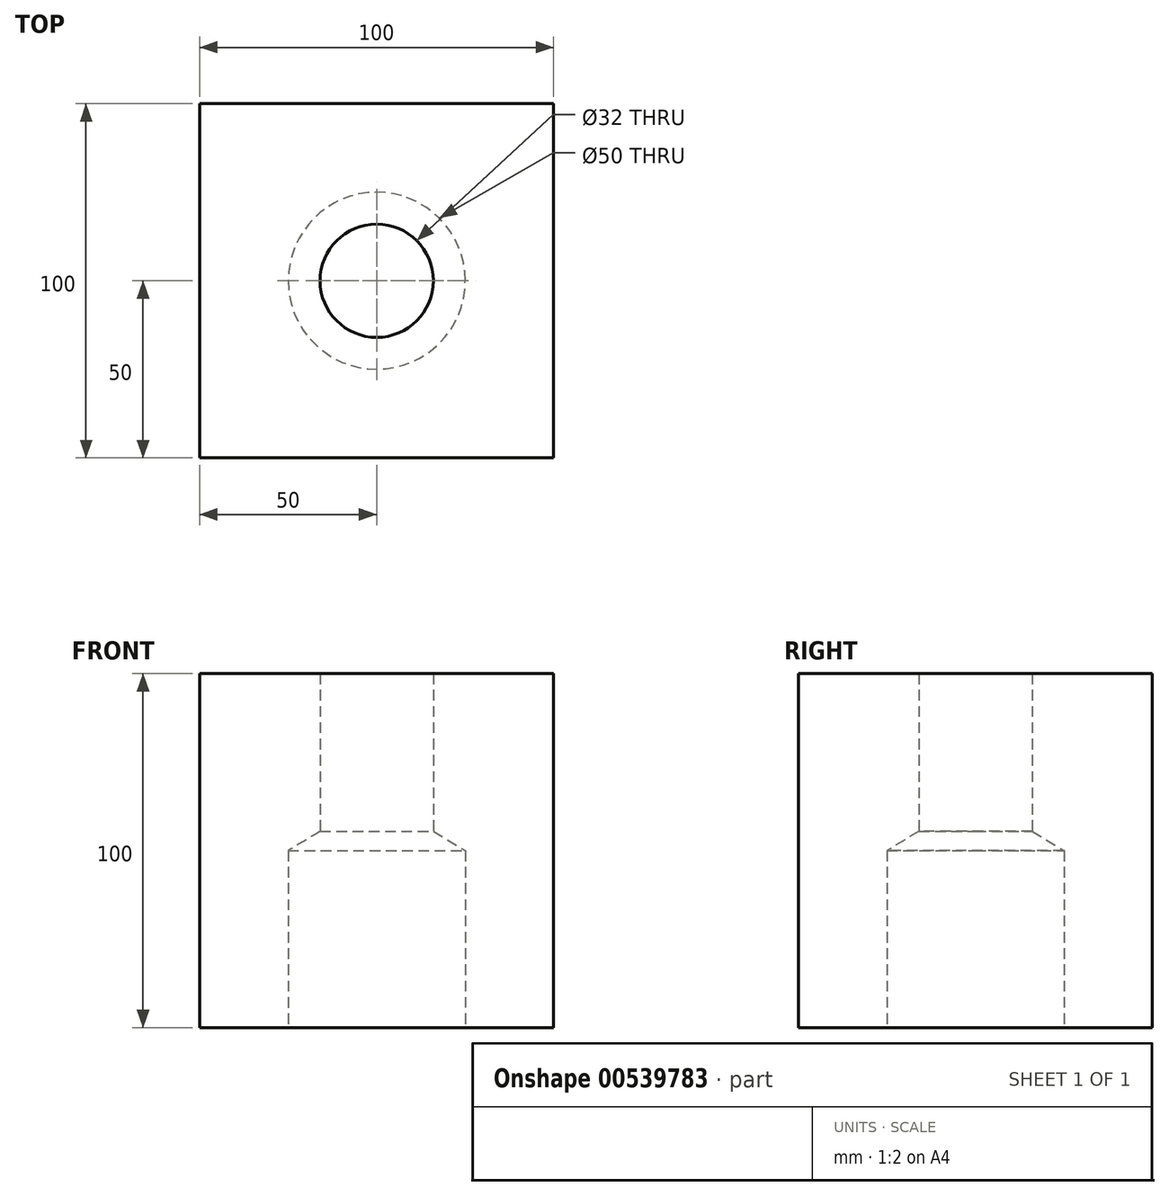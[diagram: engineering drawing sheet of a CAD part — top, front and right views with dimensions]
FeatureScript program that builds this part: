
annotation { "Feature Type Name" : "Feature", "Feature Type Description" : "" }
export const myFeature = defineFeature(function(context is Context, id is Id, definition is map)
    precondition{}
    {
        {
            var Q0;
            Q0=qCreatedBy(makeId("Top.planeOp"),FACE);
            var sketch = newSketch(context, id + "F0", { "sketchPlane" : qUnion([Q0])});
            skLineSegment(sketch, "E0.bottom", {"start": v(50, -50) * mm, "end": v(-50, -50) * mm});
            skLineSegment(sketch, "E0.top", {"start": v(50, 50) * mm, "end": v(-50, 50) * mm});
            skLineSegment(sketch, "E0.left", {"start": v(50, -50) * mm, "end": v(50, 50) * mm});
            skLineSegment(sketch, "E0.right", {"start": v(-50, -50) * mm, "end": v(-50, 50) * mm});
            skPoint(sketch, "E0.middle", {"position": v(0, 0) * mm});
            skSolve(sketch);
        }
        {
            var Q0;
            Q0 = qSketchRegion(id + "F0", true);
            extrude(context, id + "F1", {"entities" : qUnion([Q0]), "depth" : 100 * mm, "offsetDistance" : 25 * mm});
        }
        {
            var Q0;
            Q0=sQuery(id+"F0.wireOp",VERTEX,"E0.middle");
            var Q1;
            Q1=makeQuery(id+"F1.opExtrude","SWEPT_BODY",BODY,{"disambiguationData":[OSD([sQuery(id+"F0.wireOp",EDGE,"E0.bottom"),sQuery(id+"F0.wireOp",EDGE,"E0.top"),sQuery(id+"F0.wireOp",EDGE,"E0.left"),sQuery(id+"F0.wireOp",EDGE,"E0.right")])]});
            hole(context, id + "F2", {"style" : HoleStyle.SIMPLE, "endStyle" : HoleEndStyle.THROUGH, "oppositeDirection" : true, "holeDiameter" : 32 * mm, "majorDiameter" : 5 * mm, "isTappedThrough" : true, "tappedDepth" : 12 * mm, "tapClearance" : 3, "startFromSketch" : true, "locations" : qUnion([Q0]), "scope" : qUnion([Q1])});
        }
        {
            var Q0;
            Q0=sQuery(id+"F0.wireOp",VERTEX,"E0.middle");
            var Q1;
            Q1=makeQuery(id+"F1.opExtrude","SWEPT_BODY",BODY,{"disambiguationData":[OSD([sQuery(id+"F0.wireOp",EDGE,"E0.bottom"),sQuery(id+"F0.wireOp",EDGE,"E0.top"),sQuery(id+"F0.wireOp",EDGE,"E0.left"),sQuery(id+"F0.wireOp",EDGE,"E0.right")])]});
            hole(context, id + "F3", {"style" : HoleStyle.SIMPLE, "endStyle" : HoleEndStyle.BLIND, "oppositeDirection" : true, "holeDiameter" : 50 * mm, "majorDiameter" : 5 * mm, "holeDepth" : 50 * mm, "isTappedThrough" : true, "tappedDepth" : 12 * mm, "tapClearance" : 3, "locations" : qUnion([Q0]), "scope" : qUnion([Q1])});
        }
    });
